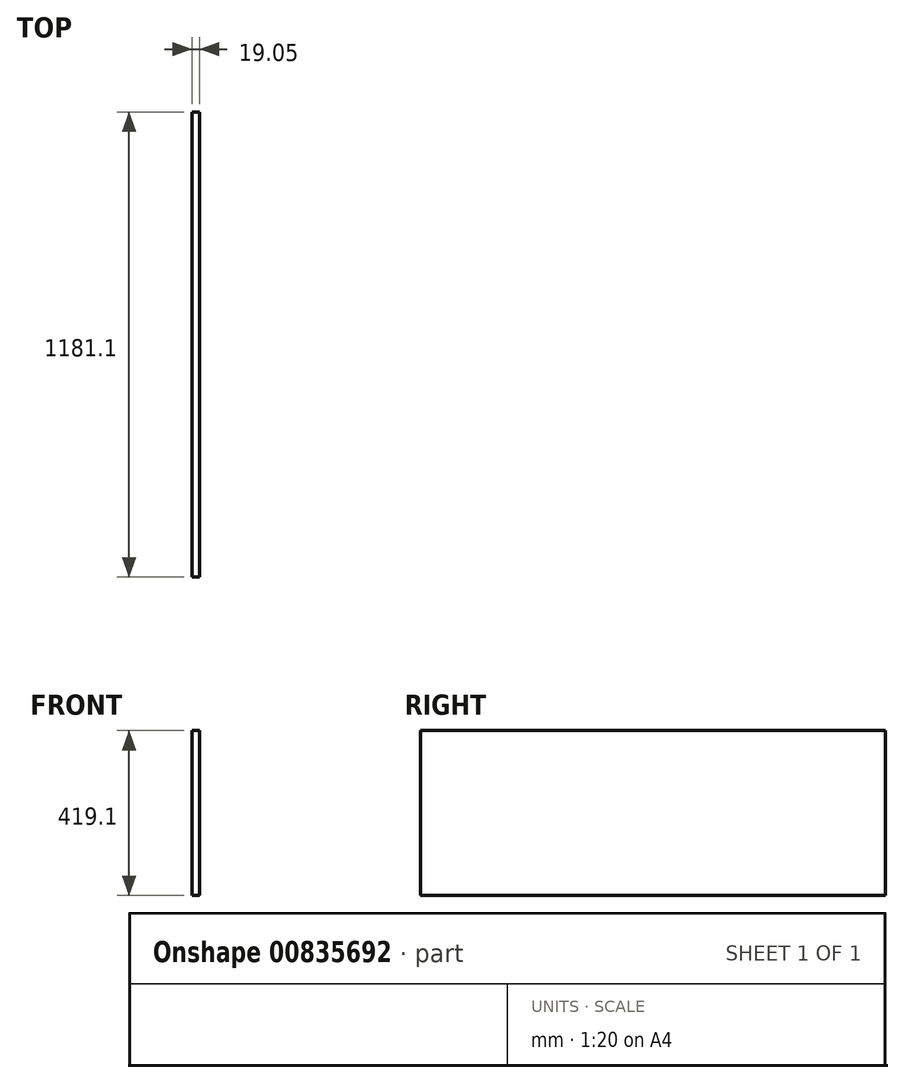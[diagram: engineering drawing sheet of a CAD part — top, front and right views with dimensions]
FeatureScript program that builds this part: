
annotation { "Feature Type Name" : "Feature", "Feature Type Description" : "" }
export const myFeature = defineFeature(function(context is Context, id is Id, definition is map)
    precondition{}
    {
        {
            var Q0;
            Q0=qCreatedBy(makeId("Right.planeOp"),FACE);
            var sketch = newSketch(context, id + "F0", { "sketchPlane" : qUnion([Q0])});
            skLineSegment(sketch, "E0.bottom", {"start": v(0, 0) * mm, "end": v(1181.1, 0) * mm});
            skLineSegment(sketch, "E0.top", {"start": v(0, 419.1) * mm, "end": v(1181.1, 419.1) * mm});
            skLineSegment(sketch, "E0.left", {"start": v(0, 0) * mm, "end": v(0, 419.1) * mm});
            skLineSegment(sketch, "E0.right", {"start": v(1181.1, 0) * mm, "end": v(1181.1, 419.1) * mm});
            skSolve(sketch);
        }
        {
            var Q0;
            Q0=qSketchRegion(id+"F0",true);
            extrude(context, id + "F1", {"entities" : qUnion([Q0]), "depth" : 19.05 * mm, "offsetDistance" : 25.4 * mm});
        }
    });
